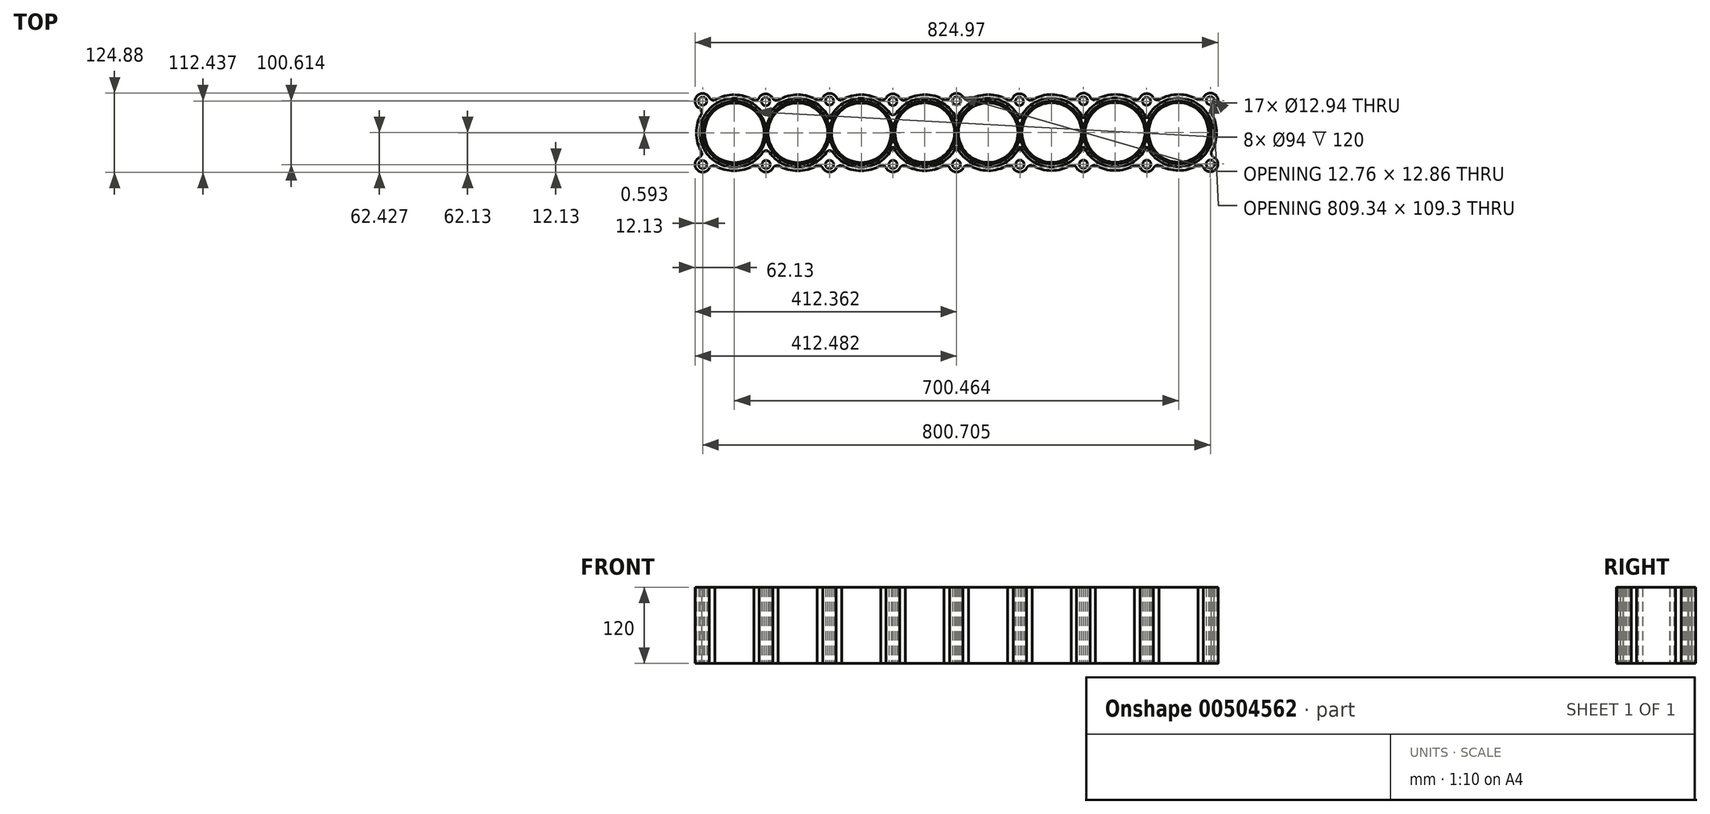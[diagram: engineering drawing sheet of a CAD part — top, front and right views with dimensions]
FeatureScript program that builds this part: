
annotation { "Feature Type Name" : "Feature", "Feature Type Description" : "" }
export const myFeature = defineFeature(function(context is Context, id is Id, definition is map)
    precondition{}
    {
        {
            var Q0;
            Q0=qCreatedBy(makeId("Top.planeOp"),FACE);
            var sketch = newSketch(context, id + "F0", { "sketchPlane" : qUnion([Q0])});
            skCircle(sketch, "E0", {"center": v(0, 0) * mm, "radius": 47 * mm});
            skCircle(sketch, "E1", {"center": v(0, 0) * mm, "radius": 50 * mm});
            skArc(sketch, "E2", {"start": v(-51.36, 31.02) * mm, "mid": v(-60, 0.03) * mm, "end": v(-51.4, -30.96) * mm});
            skCircle(sketch, "E3", {"center": v(-50, 50) * mm, "radius": 6.47 * mm});
            skArc(sketch, "E4", {"start": v(-39.13, 55.38) * mm, "mid": v(-58.24, 58.9) * mm, "end": v(-56.2, 39.57) * mm});
            skArc(sketch, "E5", {"start": v(44.78, 30.96) * mm, "mid": v(-54.44, -0.05) * mm, "end": v(44.83, -30.88) * mm});
            skCircle(sketch, "E6", {"center": v(50.07, -49.92) * mm, "radius": 6.47 * mm});
            skArc(sketch, "E7", {"start": v(39.22, -55.35) * mm, "mid": v(49.63, -62.04) * mm, "end": v(60.5, -56.12) * mm});
            skCircle(sketch, "E8", {"center": v(-50, -50) * mm, "radius": 6.47 * mm});
            skArc(sketch, "E9", {"start": v(-55.3, -39.08) * mm, "mid": v(-58.36, -58.8) * mm, "end": v(-38.83, -54.74) * mm});
            skFitSpline(sketch, "E10", {"points": [v(-39.13, 55.38) * mm, v(-30.63, 51.6) * mm], "startDerivative": vector(6.6, -10.58) * mm, "endDerivative": vector(10.04, 1.97) * mm});
            skFitSpline(sketch, "E11", {"points": [v(-51.36, 31.02) * mm, v(-56.2, 39.57) * mm], "startDerivative": vector(-0.43, 12.47) * mm, "endDerivative": vector(-9.68, 3.31) * mm});
            skFitSpline(sketch, "E12", {"points": [v(31.3, 51.18) * mm, v(39.42, 56.27) * mm], "startDerivative": vector(10.72, -3.32) * mm, "endDerivative": vector(3.31, 9.68) * mm});
            skFitSpline(sketch, "E13", {"points": [v(39.22, -55.35) * mm, v(30.6, -51.61) * mm], "startDerivative": vector(-6.6, 10.58) * mm, "endDerivative": vector(-10.04, -1.97) * mm});
            skFitSpline(sketch, "E14", {"points": [v(-55.3, -39.08) * mm, v(-51.44, -30.72) * mm], "startDerivative": vector(10.58, 6.6) * mm, "endDerivative": vector(-1.97, 10.04) * mm});
            skFitSpline(sketch, "E15", {"points": [v(-30.86, -51.45) * mm, v(-39.57, -56.2) * mm], "startDerivative": vector(-12.47, -0.43) * mm, "endDerivative": vector(-3.31, -9.68) * mm});
            skArc(sketch, "E16.trimOffspring", {"start": v(-30.86, -51.45) * mm, "mid": v(-0.15, -60) * mm, "end": v(30.6, -51.61) * mm});
            skArc(sketch, "E17.trimOffspring", {"start": v(31.3, 51.18) * mm, "mid": v(0.4, 60) * mm, "end": v(-30.63, 51.6) * mm});
            skCircle(sketch, "E18", {"center": v(100.07, 0.08) * mm, "radius": 47 * mm});
            skCircle(sketch, "E19", {"center": v(100.07, 0.08) * mm, "radius": 50 * mm});
            skCircle(sketch, "E20", {"center": v(49.32, 49.27) * mm, "radius": 6.47 * mm});
            skArc(sketch, "E21", {"start": v(60.47, 54.05) * mm, "mid": v(49.19, 61.4) * mm, "end": v(38.07, 53.8) * mm});
            skArc(sketch, "E22", {"start": v(55.29, -30.87) * mm, "mid": v(100.11, -54.35) * mm, "end": v(144.9, -30.8) * mm});
            skArc(sketch, "E23", {"start": v(161.12, 55.6) * mm, "mid": v(149.8, 62.23) * mm, "end": v(139.07, 54.69) * mm});
            skCircle(sketch, "E24", {"center": v(150.13, -49.83) * mm, "radius": 6.47 * mm});
            skArc(sketch, "E25", {"start": v(139.29, -55.27) * mm, "mid": v(149.7, -61.95) * mm, "end": v(160.56, -56.03) * mm});
            skFitSpline(sketch, "E26", {"points": [v(60.47, 54.05) * mm, v(69.44, 51.68) * mm], "startDerivative": vector(6.6, -10.58) * mm, "endDerivative": vector(10.04, 1.97) * mm});
            skFitSpline(sketch, "E27", {"points": [v(131.38, 51.27) * mm, v(139.8, 56.18) * mm], "startDerivative": vector(12.47, 0.43) * mm, "endDerivative": vector(3.31, 9.68) * mm});
            skFitSpline(sketch, "E28", {"points": [v(139.29, -55.27) * mm, v(130.67, -51.53) * mm], "startDerivative": vector(-6.6, 10.58) * mm, "endDerivative": vector(-10.04, -1.97) * mm});
            skFitSpline(sketch, "E29", {"points": [v(69.2, -51.37) * mm, v(60.5, -56.12) * mm], "startDerivative": vector(-12.47, -0.43) * mm, "endDerivative": vector(-3.31, -9.68) * mm});
            skArc(sketch, "E30.trimOffspring", {"start": v(69.2, -51.37) * mm, "mid": v(99.91, -59.92) * mm, "end": v(130.67, -51.53) * mm});
            skArc(sketch, "E31.trimOffspring", {"start": v(131.38, 51.27) * mm, "mid": v(100.46, 60.08) * mm, "end": v(69.44, 51.68) * mm});
            skCircle(sketch, "E32", {"center": v(200.13, 0.17) * mm, "radius": 47 * mm});
            skCircle(sketch, "E33", {"center": v(200.13, 0.17) * mm, "radius": 50 * mm});
            skCircle(sketch, "E34", {"center": v(150.13, 50.17) * mm, "radius": 6.47 * mm});
            skArc(sketch, "E35", {"start": v(244.91, 31.13) * mm, "mid": v(194.68, 54.33) * mm, "end": v(150.08, 21.58) * mm});
            skCircle(sketch, "E36", {"center": v(250.2, -49.75) * mm, "radius": 6.47 * mm});
            skArc(sketch, "E37", {"start": v(239.36, -55.18) * mm, "mid": v(250.59, -61.87) * mm, "end": v(261.37, -54.48) * mm});
            skFitSpline(sketch, "E38", {"points": [v(161.12, 55.6) * mm, v(169.5, 51.76) * mm], "startDerivative": vector(6.6, -10.58) * mm, "endDerivative": vector(10.04, 1.97) * mm});
            skFitSpline(sketch, "E39", {"points": [v(231.44, 51.35) * mm, v(239.87, 56.27) * mm], "startDerivative": vector(12.47, 0.43) * mm, "endDerivative": vector(3.31, 9.68) * mm});
            skFitSpline(sketch, "E40", {"points": [v(239.36, -55.18) * mm, v(230.73, -51.44) * mm], "startDerivative": vector(-6.6, 10.58) * mm, "endDerivative": vector(-10.04, -1.97) * mm});
            skFitSpline(sketch, "E41", {"points": [v(169.27, -51.28) * mm, v(160.56, -56.03) * mm], "startDerivative": vector(-12.47, -0.43) * mm, "endDerivative": vector(-3.31, -9.68) * mm});
            skArc(sketch, "E42.trimOffspring", {"start": v(169.27, -51.28) * mm, "mid": v(199.98, -59.83) * mm, "end": v(230.73, -51.44) * mm});
            skArc(sketch, "E43.trimOffspring", {"start": v(231.44, 51.35) * mm, "mid": v(200.53, 60.17) * mm, "end": v(169.5, 51.76) * mm});
            skCircle(sketch, "E44", {"center": v(300.2, 0.25) * mm, "radius": 47 * mm});
            skCircle(sketch, "E45", {"center": v(300.2, 0.25) * mm, "radius": 50 * mm});
            skCircle(sketch, "E46", {"center": v(249.85, 49.37) * mm, "radius": 6.47 * mm});
            skArc(sketch, "E47", {"start": v(260.72, 54.75) * mm, "mid": v(249.57, 61.5) * mm, "end": v(238.74, 54.23) * mm});
            skArc(sketch, "E48", {"start": v(250.18, -21.24) * mm, "mid": v(300.25, -54.18) * mm, "end": v(350.25, -21.16) * mm});
            skArc(sketch, "E49", {"start": v(352.56, 56.39) * mm, "mid": v(344.36, 52.48) * mm, "end": v(348.15, 44.22) * mm});
            skCircle(sketch, "E50", {"center": v(350.27, -49.66) * mm, "radius": 6.47 * mm});
            skArc(sketch, "E51", {"start": v(339.42, -55.1) * mm, "mid": v(349.83, -61.78) * mm, "end": v(360.7, -55.86) * mm});
            skFitSpline(sketch, "E52", {"points": [v(260.72, 54.75) * mm, v(269.57, 51.85) * mm], "startDerivative": vector(6.6, -10.58) * mm, "endDerivative": vector(10.04, 1.97) * mm});
            skFitSpline(sketch, "E53", {"points": [v(331.5, 51.44) * mm, v(339.94, 56.35) * mm], "startDerivative": vector(12.47, 0.43) * mm, "endDerivative": vector(3.31, 9.68) * mm});
            skFitSpline(sketch, "E54", {"points": [v(339.42, -55.1) * mm, v(330.8, -51.36) * mm], "startDerivative": vector(-6.6, 10.58) * mm, "endDerivative": vector(-10.04, -1.97) * mm});
            skFitSpline(sketch, "E55", {"points": [v(269.34, -51.2) * mm, v(260.63, -55.95) * mm], "startDerivative": vector(-12.47, -0.43) * mm, "endDerivative": vector(-3.31, -9.68) * mm});
            skArc(sketch, "E56.trimOffspring", {"start": v(269.34, -51.2) * mm, "mid": v(300.05, -59.75) * mm, "end": v(330.8, -51.36) * mm});
            skArc(sketch, "E57.trimOffspring", {"start": v(331.5, 51.44) * mm, "mid": v(300.6, 60.25) * mm, "end": v(269.57, 51.85) * mm});
            skArc(sketch, "E58.trimOffspring", {"start": v(150.08, 21.58) * mm, "mid": v(105.43, 54.26) * mm, "end": v(55.23, 30.96) * mm});
            skArc(sketch, "E59.trimOffspring", {"start": v(155.35, -30.79) * mm, "mid": v(205.58, -54) * mm, "end": v(250.18, -21.24) * mm});
            skCircle(sketch, "E60", {"center": v(400.27, 0.34) * mm, "radius": 47 * mm});
            skCircle(sketch, "E61", {"center": v(400.27, 0.34) * mm, "radius": 50 * mm});
            skArc(sketch, "E62", {"start": v(348.15, 44.22) * mm, "mid": v(356.35, 48.13) * mm, "end": v(352.56, 56.39) * mm});
            skArc(sketch, "E63", {"start": v(361.14, 55.72) * mm, "mid": v(358.39, 59.35) * mm, "end": v(354.49, 61.71) * mm});
            skArc(sketch, "E64", {"start": v(450.28, 21.83) * mm, "mid": v(400.22, 54.78) * mm, "end": v(350.21, 21.75) * mm});
            skCircle(sketch, "E65", {"center": v(450.33, -49.58) * mm, "radius": 6.47 * mm});
            skArc(sketch, "E66", {"start": v(439.49, -55.02) * mm, "mid": v(449.9, -61.7) * mm, "end": v(460.76, -55.78) * mm});
            skFitSpline(sketch, "E67", {"points": [v(361.14, 55.72) * mm, v(369.64, 51.93) * mm], "startDerivative": vector(6.6, -10.58) * mm, "endDerivative": vector(10.04, 1.97) * mm});
            skFitSpline(sketch, "E68", {"points": [v(431.57, 51.52) * mm, v(439.68, 56.61) * mm], "startDerivative": vector(10.72, -3.32) * mm, "endDerivative": vector(3.31, 9.68) * mm});
            skFitSpline(sketch, "E69", {"points": [v(439.49, -55.02) * mm, v(430.86, -51.27) * mm], "startDerivative": vector(-6.6, 10.58) * mm, "endDerivative": vector(-10.04, -1.97) * mm});
            skFitSpline(sketch, "E70", {"points": [v(369.4, -51.11) * mm, v(360.7, -55.86) * mm], "startDerivative": vector(-12.47, -0.43) * mm, "endDerivative": vector(-3.31, -9.68) * mm});
            skArc(sketch, "E71.trimOffspring", {"start": v(369.4, -51.11) * mm, "mid": v(400.11, -59.66) * mm, "end": v(430.86, -51.27) * mm});
            skArc(sketch, "E72.trimOffspring", {"start": v(431.57, 51.52) * mm, "mid": v(400.66, 60.34) * mm, "end": v(369.64, 51.93) * mm});
            skCircle(sketch, "E73", {"center": v(500.33, 0.42) * mm, "radius": 47 * mm});
            skCircle(sketch, "E74", {"center": v(500.33, 0.42) * mm, "radius": 50 * mm});
            skCircle(sketch, "E75", {"center": v(449.58, 49.6) * mm, "radius": 6.47 * mm});
            skArc(sketch, "E76", {"start": v(460.73, 54.39) * mm, "mid": v(449.45, 61.74) * mm, "end": v(438.33, 54.15) * mm});
            skArc(sketch, "E77", {"start": v(450.32, -21.07) * mm, "mid": v(500.38, -54.01) * mm, "end": v(550.38, -20.99) * mm});
            skArc(sketch, "E78", {"start": v(561.38, 55.95) * mm, "mid": v(550.07, 62.57) * mm, "end": v(539.34, 55.02) * mm});
            skCircle(sketch, "E79", {"center": v(550.4, -49.5) * mm, "radius": 6.47 * mm});
            skArc(sketch, "E80", {"start": v(539.55, -54.93) * mm, "mid": v(549.96, -61.61) * mm, "end": v(560.82, -55.7) * mm});
            skFitSpline(sketch, "E81", {"points": [v(460.73, 54.39) * mm, v(469.7, 52.02) * mm], "startDerivative": vector(6.6, -10.58) * mm, "endDerivative": vector(10.04, 1.97) * mm});
            skFitSpline(sketch, "E82", {"points": [v(531.64, 51.6) * mm, v(540.07, 56.52) * mm], "startDerivative": vector(12.47, 0.43) * mm, "endDerivative": vector(3.31, 9.68) * mm});
            skFitSpline(sketch, "E83", {"points": [v(539.55, -54.93) * mm, v(530.93, -51.19) * mm], "startDerivative": vector(-6.6, 10.58) * mm, "endDerivative": vector(-10.04, -1.97) * mm});
            skFitSpline(sketch, "E84", {"points": [v(469.47, -51.03) * mm, v(460.76, -55.78) * mm], "startDerivative": vector(-12.47, -0.43) * mm, "endDerivative": vector(-3.31, -9.68) * mm});
            skArc(sketch, "E85.trimOffspring", {"start": v(469.47, -51.03) * mm, "mid": v(500.18, -59.58) * mm, "end": v(530.93, -51.19) * mm});
            skArc(sketch, "E86.trimOffspring", {"start": v(531.64, 51.6) * mm, "mid": v(500.73, 60.42) * mm, "end": v(469.7, 52.02) * mm});
            skCircle(sketch, "E87", {"center": v(600.4, 0.5) * mm, "radius": 47 * mm});
            skCircle(sketch, "E88", {"center": v(600.4, 0.5) * mm, "radius": 50 * mm});
            skCircle(sketch, "E89", {"center": v(550.4, 50.5) * mm, "radius": 6.47 * mm});
            skArc(sketch, "E90", {"start": v(650.41, 22) * mm, "mid": v(600.35, 54.95) * mm, "end": v(550.35, 21.92) * mm});
            skCircle(sketch, "E91", {"center": v(650.46, -49.4) * mm, "radius": 6.47 * mm});
            skArc(sketch, "E92", {"start": v(639.62, -54.85) * mm, "mid": v(650.85, -61.53) * mm, "end": v(661.63, -54.14) * mm});
            skFitSpline(sketch, "E93", {"points": [v(561.38, 55.95) * mm, v(569.77, 52.1) * mm], "startDerivative": vector(6.6, -10.58) * mm, "endDerivative": vector(10.04, 1.97) * mm});
            skFitSpline(sketch, "E94", {"points": [v(631.7, 51.7) * mm, v(640.14, 56.6) * mm], "startDerivative": vector(12.47, 0.43) * mm, "endDerivative": vector(3.31, 9.68) * mm});
            skFitSpline(sketch, "E95", {"points": [v(639.62, -54.85) * mm, v(631, -51.1) * mm], "startDerivative": vector(-6.6, 10.58) * mm, "endDerivative": vector(-10.04, -1.97) * mm});
            skFitSpline(sketch, "E96", {"points": [v(569.53, -50.95) * mm, v(560.82, -55.7) * mm], "startDerivative": vector(-12.47, -0.43) * mm, "endDerivative": vector(-3.31, -9.68) * mm});
            skArc(sketch, "E97.trimOffspring", {"start": v(569.53, -50.95) * mm, "mid": v(600.24, -59.5) * mm, "end": v(631, -51.1) * mm});
            skArc(sketch, "E98.trimOffspring", {"start": v(631.7, 51.7) * mm, "mid": v(600.8, 60.5) * mm, "end": v(569.77, 52.1) * mm});
            skCircle(sketch, "E99", {"center": v(700.46, 0.6) * mm, "radius": 47 * mm});
            skCircle(sketch, "E100", {"center": v(700.46, 0.6) * mm, "radius": 50 * mm});
            skCircle(sketch, "E101", {"center": v(650.12, 49.7) * mm, "radius": 6.47 * mm});
            skArc(sketch, "E102", {"start": v(660.99, 55.09) * mm, "mid": v(649.83, 61.83) * mm, "end": v(639, 54.57) * mm});
            skArc(sketch, "E103", {"start": v(650.45, -20.9) * mm, "mid": v(754.9, 0.64) * mm, "end": v(650.41, 22) * mm});
            skCircle(sketch, "E104", {"center": v(750.7, 50.61) * mm, "radius": 6.47 * mm});
            skArc(sketch, "E105", {"start": v(756.03, 39.71) * mm, "mid": v(759, 59.47) * mm, "end": v(739.47, 55.2) * mm});
            skCircle(sketch, "E106", {"center": v(750.53, -49.32) * mm, "radius": 6.47 * mm});
            skArc(sketch, "E107", {"start": v(739.69, -54.76) * mm, "mid": v(759.42, -57.57) * mm, "end": v(755.15, -38.1) * mm});
            skFitSpline(sketch, "E108", {"points": [v(660.99, 55.09) * mm, v(669.84, 52.19) * mm], "startDerivative": vector(6.6, -10.58) * mm, "endDerivative": vector(10.04, 1.97) * mm});
            skFitSpline(sketch, "E109", {"points": [v(756.03, 39.71) * mm, v(752.21, 30.96) * mm], "startDerivative": vector(-10.58, -6.6) * mm, "endDerivative": vector(1.97, -10.04) * mm});
            skFitSpline(sketch, "E110", {"points": [v(731.77, 51.78) * mm, v(740.2, 56.69) * mm], "startDerivative": vector(12.47, 0.43) * mm, "endDerivative": vector(3.31, 9.68) * mm});
            skFitSpline(sketch, "E111", {"points": [v(739.69, -54.76) * mm, v(731.06, -51.02) * mm], "startDerivative": vector(-6.6, 10.58) * mm, "endDerivative": vector(-10.04, -1.97) * mm});
            skFitSpline(sketch, "E112", {"points": [v(751.8, -30.46) * mm, v(756.72, -38.89) * mm], "startDerivative": vector(0.43, -12.47) * mm, "endDerivative": vector(9.68, -3.31) * mm});
            skFitSpline(sketch, "E113", {"points": [v(669.6, -50.86) * mm, v(660.9, -55.6) * mm], "startDerivative": vector(-12.47, -0.43) * mm, "endDerivative": vector(-3.31, -9.68) * mm});
            skArc(sketch, "E114.trimOffspring", {"start": v(751.8, -30.46) * mm, "mid": v(760.46, 0.2) * mm, "end": v(752.21, 30.96) * mm});
            skArc(sketch, "E115.trimOffspring", {"start": v(669.6, -50.86) * mm, "mid": v(700.31, -59.4) * mm, "end": v(731.06, -51.02) * mm});
            skArc(sketch, "E116.trimOffspring", {"start": v(731.77, 51.78) * mm, "mid": v(700.86, 60.6) * mm, "end": v(669.84, 52.19) * mm});
            skArc(sketch, "E117.trimOffspring", {"start": v(550.35, 21.92) * mm, "mid": v(500.29, 54.86) * mm, "end": v(450.28, 21.83) * mm});
            skArc(sketch, "E118.trimOffspring", {"start": v(550.38, -20.99) * mm, "mid": v(600.44, -53.93) * mm, "end": v(650.45, -20.9) * mm});
            skArc(sketch, "E119.trimOffspring", {"start": v(354.49, 61.71) * mm, "mid": v(345.47, 61.34) * mm, "end": v(339.2, 54.86) * mm});
            skArc(sketch, "E120.trimOffspring", {"start": v(350.21, 21.75) * mm, "mid": v(305.56, 54.43) * mm, "end": v(255.37, 31.13) * mm});
            skArc(sketch, "E121.trimOffspring", {"start": v(350.25, -21.16) * mm, "mid": v(400.31, -54.1) * mm, "end": v(450.32, -21.07) * mm});
            skPoint(sketch, "E122.visualSharp", {"position": v(50.01, 21.5) * mm});
            skArc(sketch, "E122.filletArc", {"start": v(44.78, 30.96) * mm, "mid": v(50, 28.22) * mm, "end": v(55.23, 30.96) * mm});
            skPoint(sketch, "E123.visualSharp", {"position": v(50.05, -21.41) * mm});
            skArc(sketch, "E123.filletArc", {"start": v(55.29, -30.87) * mm, "mid": v(50.06, -28.13) * mm, "end": v(44.83, -30.88) * mm});
            skPoint(sketch, "E124.visualSharp", {"position": v(150.12, -21.33) * mm});
            skArc(sketch, "E124.filletArc", {"start": v(155.35, -30.79) * mm, "mid": v(150.12, -28.05) * mm, "end": v(144.9, -30.8) * mm});
            skPoint(sketch, "E125.visualSharp", {"position": v(250.15, 21.66) * mm});
            skArc(sketch, "E125.filletArc", {"start": v(244.91, 31.13) * mm, "mid": v(250.14, 28.39) * mm, "end": v(255.37, 31.13) * mm});
            skSolve(sketch);
        }
        {
            var Q0;
            {var subQ15=sQuery(id+"F0.wireOp",EDGE,"E2");Q0=makeQuery(id+"F0.imprint","IMPRINT",FACE,{"disambiguationData":[TD([[makeQuery(id+"F0.imprint","IMPRINT",EDGE,{"derivedFrom":subQ15}),1.0]])]});}
            var Q1;
            Q1=makeQuery(id+"F0.imprint","IMPRINT",FACE,{"disambiguationData":[TD([[makeQuery(id+"F0.imprint","IMPRINT",EDGE,{"derivedFrom":sQuery(id+"F0.wireOp",EDGE,"E0")}),-1.0]])]});
            var Q2;
            Q2=makeQuery(id+"F0.imprint","IMPRINT",FACE,{"disambiguationData":[TD([[makeQuery(id+"F0.imprint","IMPRINT",EDGE,{"derivedFrom":sQuery(id+"F0.wireOp",EDGE,"E18")}),-1.0]])]});
            var Q3;
            Q3=makeQuery(id+"F0.imprint","IMPRINT",FACE,{"disambiguationData":[TD([[makeQuery(id+"F0.imprint","IMPRINT",EDGE,{"derivedFrom":sQuery(id+"F0.wireOp",EDGE,"E32")}),-1.0]])]});
            var Q4;
            Q4=makeQuery(id+"F0.imprint","IMPRINT",FACE,{"disambiguationData":[TD([[makeQuery(id+"F0.imprint","IMPRINT",EDGE,{"derivedFrom":sQuery(id+"F0.wireOp",EDGE,"E44")}),-1.0]])]});
            var Q5;
            Q5=makeQuery(id+"F0.imprint","IMPRINT",FACE,{"disambiguationData":[TD([[makeQuery(id+"F0.imprint","IMPRINT",EDGE,{"derivedFrom":sQuery(id+"F0.wireOp",EDGE,"E60")}),-1.0]])]});
            var Q6;
            Q6=makeQuery(id+"F0.imprint","IMPRINT",FACE,{"disambiguationData":[TD([[makeQuery(id+"F0.imprint","IMPRINT",EDGE,{"derivedFrom":sQuery(id+"F0.wireOp",EDGE,"E73")}),-1.0]])]});
            var Q7;
            Q7=makeQuery(id+"F0.imprint","IMPRINT",FACE,{"disambiguationData":[TD([[makeQuery(id+"F0.imprint","IMPRINT",EDGE,{"derivedFrom":sQuery(id+"F0.wireOp",EDGE,"E87")}),-1.0]])]});
            var Q8;
            Q8=makeQuery(id+"F0.imprint","IMPRINT",FACE,{"disambiguationData":[TD([[makeQuery(id+"F0.imprint","IMPRINT",EDGE,{"derivedFrom":sQuery(id+"F0.wireOp",EDGE,"E99")}),-1.0]])]});
            extrude(context, id + "F1", {"entities" : qUnion([Q0, Q1, Q2, Q3, Q4, Q5, Q6, Q7, Q8]), "offsetDistance" : 25.4 * mm, "depth" : 120 * mm});
        }
    });
